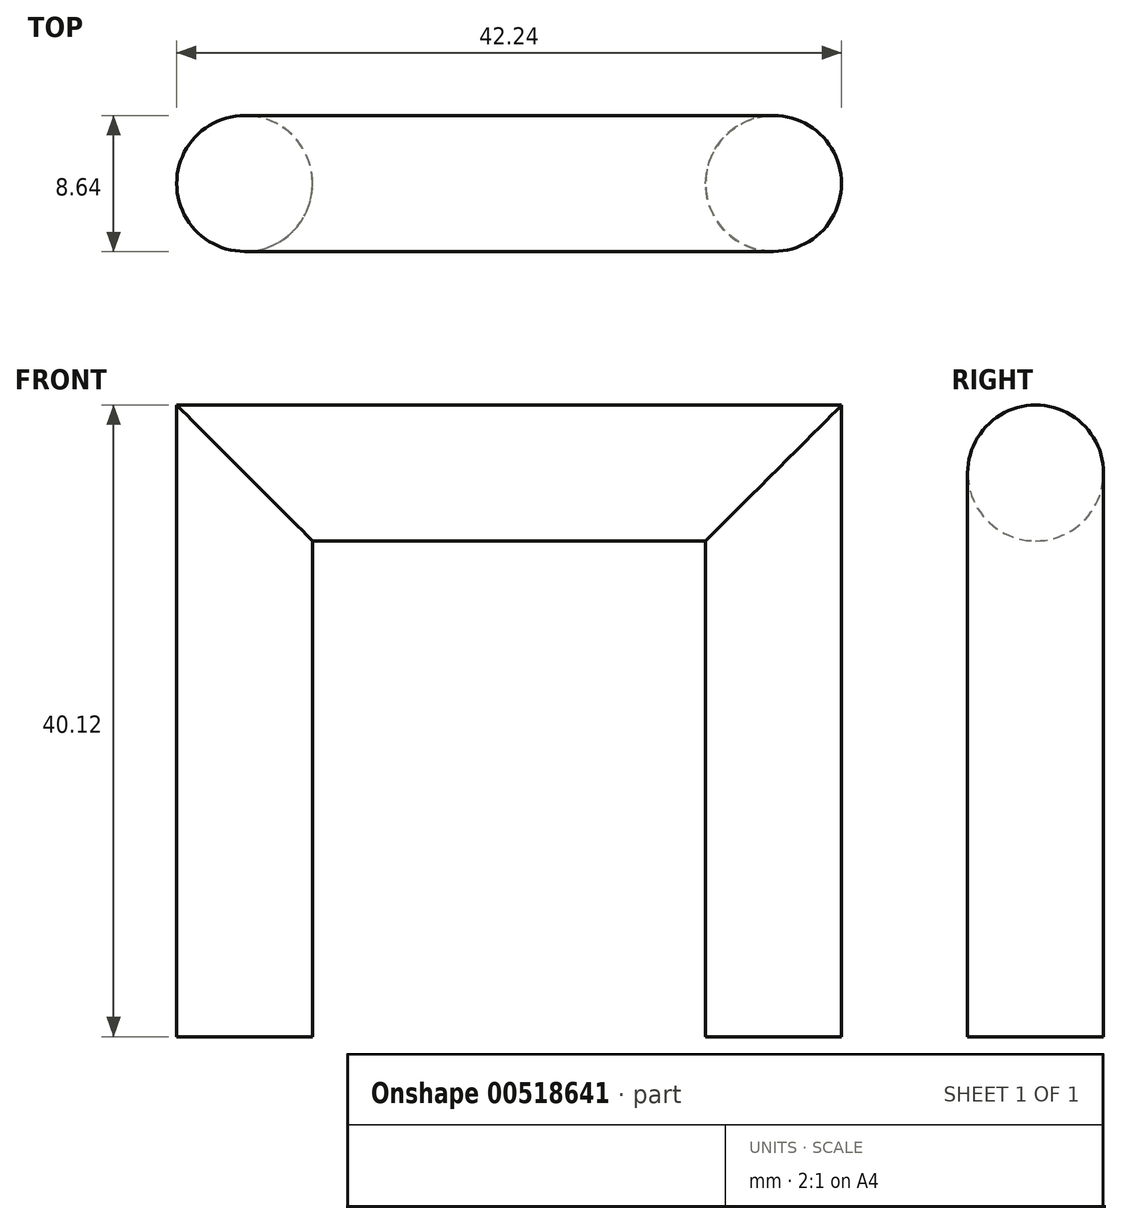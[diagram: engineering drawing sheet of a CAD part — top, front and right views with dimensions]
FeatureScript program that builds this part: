
annotation { "Feature Type Name" : "Feature", "Feature Type Description" : "" }
export const myFeature = defineFeature(function(context is Context, id is Id, definition is map)
    precondition{}
    {
        {
            var Q0;
            Q0=qCreatedBy(makeId("Front.planeOp"),FACE);
            var sketch = newSketch(context, id + "F0", { "sketchPlane" : qUnion([Q0])});
            skLineSegment(sketch, "E0", {"start": v(0, 0) * mm, "end": v(0, 35.8) * mm});
            skLineSegment(sketch, "E1", {"start": v(0, 35.8) * mm, "end": v(33.6, 35.8) * mm});
            skLineSegment(sketch, "E2", {"start": v(33.6, 35.8) * mm, "end": v(33.6, 0) * mm});
            skSolve(sketch);
        }
        {
            var Q0;
            Q0=qCreatedBy(makeId("Top.planeOp"),FACE);
            var sketch = newSketch(context, id + "F1", { "sketchPlane" : qUnion([Q0])});
            skCircle(sketch, "E3", {"center": v(0, 0) * mm, "radius": 4.32 * mm});
            skSolve(sketch);
        }
        {
            var Q0;
            Q0=makeQuery(id+"F1.imprint","IMPRINT",FACE,{"disambiguationData":[TD([[makeQuery(id+"F1.imprint","IMPRINT",EDGE,{"derivedFrom":sQuery(id+"F1.wireOp",EDGE,"E3")}),1.0]])]});
            var Q1;
            Q1=sQuery(id+"F0.wireOp",EDGE,"E0");
            var Q2;
            Q2=sQuery(id+"F0.wireOp",EDGE,"E1");
            var Q3;
            Q3=sQuery(id+"F0.wireOp",EDGE,"E2");
            sweep(context, id + "F2", {"profiles" : qUnion([Q0]), "path" : qUnion([Q1, Q2, Q3])});
        }
    });
